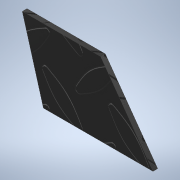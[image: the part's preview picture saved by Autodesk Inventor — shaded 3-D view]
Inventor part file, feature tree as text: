
AUTODESK INVENTOR PART (.ipt)
format: ipt  version: 2020 (Build 240168000, 168)  size: 97,280 bytes
history: native  units: mm
features: extrude x1, sketch x1
ambient origin geometry x8: Origin, YZ Plane, XZ Plane, XY Plane, X Axis, Y Axis, Z Axis, Center Point
bodies: Solid1 (feature_tree)
feature tree (2):
  extrude  "Extrusion1"  Depth=3.0mm
  sketch  "Sketch1"  dims[d0=70.0mm d1=57.5mm d2=9.494591mm d3=50.0mm d4=3.0mm d5=0.0mm]
